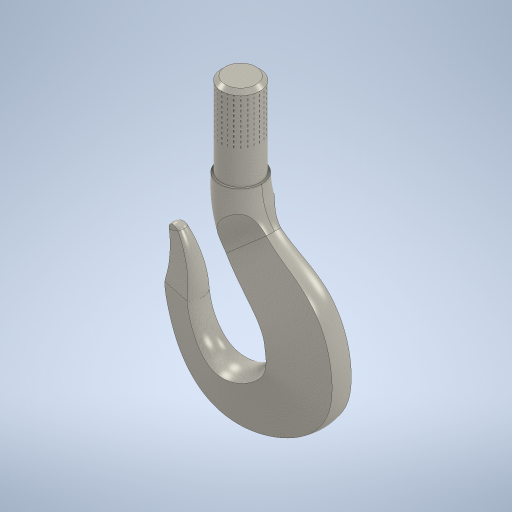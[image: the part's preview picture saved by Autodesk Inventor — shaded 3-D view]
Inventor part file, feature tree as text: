
AUTODESK INVENTOR PART (.ipt)
format: ipt  version: 2024 (Build 280153000, 153)  size: 758,784 bytes
history: native  units: mm
features: other x20, plane x15, sketch x4, loft x3, extrude x3, boolean_combine x2, mirror x1, thread x1, chamfer x1, revolve x1, projected_geometry x1
ambient origin geometry x8: Origin, YZ Plane, XZ Plane, XY Plane, X Axis, Y Axis, Z Axis, Center Point
bodies: Solid1 (feature_tree), Solid2 (feature_tree), Solid3 (feature_tree)
feature tree (52):
  other  "Basic Sketch"
  plane  "Work Plane1"
  plane  "Work Plane2"
  plane  "Work Plane3"
  plane  "Work Plane4"
  plane  "Work Plane5"
  plane  "Work Plane6"
  plane  "Work Plane7"
  plane  "Work Plane8"
  plane  "Work Plane10"
  other  "Section 1"
  loft  "Loft1"
  loft  "Loft2"
  other  "Segment 3"
  plane  "Work Plane11"
  plane  "Work Plane12"
  plane  "Work Plane13"
  plane  "Work Plane14"
  plane  "Work Plane15"
  loft  "Loft3"
  other  "Work Axis1"
  other  "Work Point1"
  plane  "Work Plane16"
  extrude  "Extrusion1"  Depth=10.0mm
  mirror  "Mirror1"
  extrude  "Extrusion2"  Depth=6.0mm
  thread  "Thread1"  [1 undecoded]
  chamfer  "Chamfer1"  Distance=21.0mm
  revolve  "Revolution1"  [1 undecoded]
  extrude  "Extrusion3"  Depth=10.0mm
  boolean_combine  "Combine1"
  boolean_combine  "Combine2"
  other  "Section 2"
  other  "Section 5"
  other  "Section 3"
  other  "Section 4"
  other  "Section 6"
  other  "Section 7"
  other  "Section 8"
  other  "Section 9"
  other  "Section 1_0"
  other  "Section 10"
  other  "Section 11"
  other  "Section 12"
  other  "Section 13"
  other  "Section 14"
  other  "Section Start"
  sketch  "Sketch19"  dims[d0=33.0mm d1=100.0mm]
  sketch  "Sketch20"  dims[d2=30.0mm d3=68.0mm]
  sketch  "Sketch21"  dims[d4=12.0mm d5=42.0mm]
  sketch  "Sketch22"  dims[d6=100.0mm d7=62.0mm d8=6.0mm d9=36.0mm d10=21.0mm d11=66.0mm d12=6.981317mm d13=4.363323mm d14=4.363323mm d15=30.0deg d16=6.108652mm d17=90.0deg d18=33.0mm d19=90.0deg d20=90.0deg d21=15.0mm d22=33.0mm d24=4.161261mm d25=37.574812mm d26=24.799376mm d27=90.0deg d28=4.161261mm d29=47.156537mm d30=31.123315mm d31=90.0deg d32=4.161261mm d33=49.307455mm d34=32.54292mm d35=90.0deg d36=4.161261mm d37=48.998428mm d38=32.338962mm d39=90.0deg d40=4.161261mm d41=36.932802mm d42=24.375649mm d43=90.0deg d44=4.161261mm d45=27.820936mm d46=18.361818mm d47=90.0deg d48=4.161261mm d49=26.0mm d50=17.16mm d51=0.0mm d52=90.0deg d53=0.0mm d54=90.0deg d55=0.0mm d56=90.0deg d57=0.0mm d58=90.0deg d59=0.0mm d60=90.0deg d61=0.0mm d62=90.0deg d63=0.0mm d64=90.0deg d65=0.0mm d66=90.0deg d67=0.0mm d68=90.0deg d69=0.0mm d70=90.0deg d71=0.0mm d72=90.0deg d73=0.0mm d74=90.0deg d75=30.0mm d76=15.0deg d77=3.0mm d78=12.0mm d79=20.0mm d80=90.0deg d81=4.161261mm d82=25.295786mm d83=16.695219mm d84=90.0deg d85=4.161261mm d86=22.435744mm d87=14.807591mm d88=90.0deg d89=4.161261mm d90=19.805096mm d91=13.071363mm d92=90.0deg d93=4.161261mm d94=15.339196mm d95=10.123869mm d96=90.0deg d97=4.161261mm d98=11.671766mm d99=7.703366mm d100=0.0mm d101=90.0deg d102=0.0mm d103=90.0deg d104=0.0mm d105=90.0deg d106=0.0mm d107=90.0deg d108=0.0mm d109=90.0deg d110=0.0mm d111=90.0deg d112=25.0mm d113=25.0mm d114=0.0mm d115=0.0mm d116=30.0mm d117=65.0mm d118=0.0mm d119=40.0mm d120=0.0mm d121=3.0mm d122=2.0mm d123=45.0deg d124=90.0deg d125=10.0mm d126=0.0mm]
  projected_geometry  "Projected Loop1"
note: 2 required parameter values undecoded (feature->parameter linkage not recoverable at this tier; creation-order binding heuristic only, values carry confidence <= 0.55)